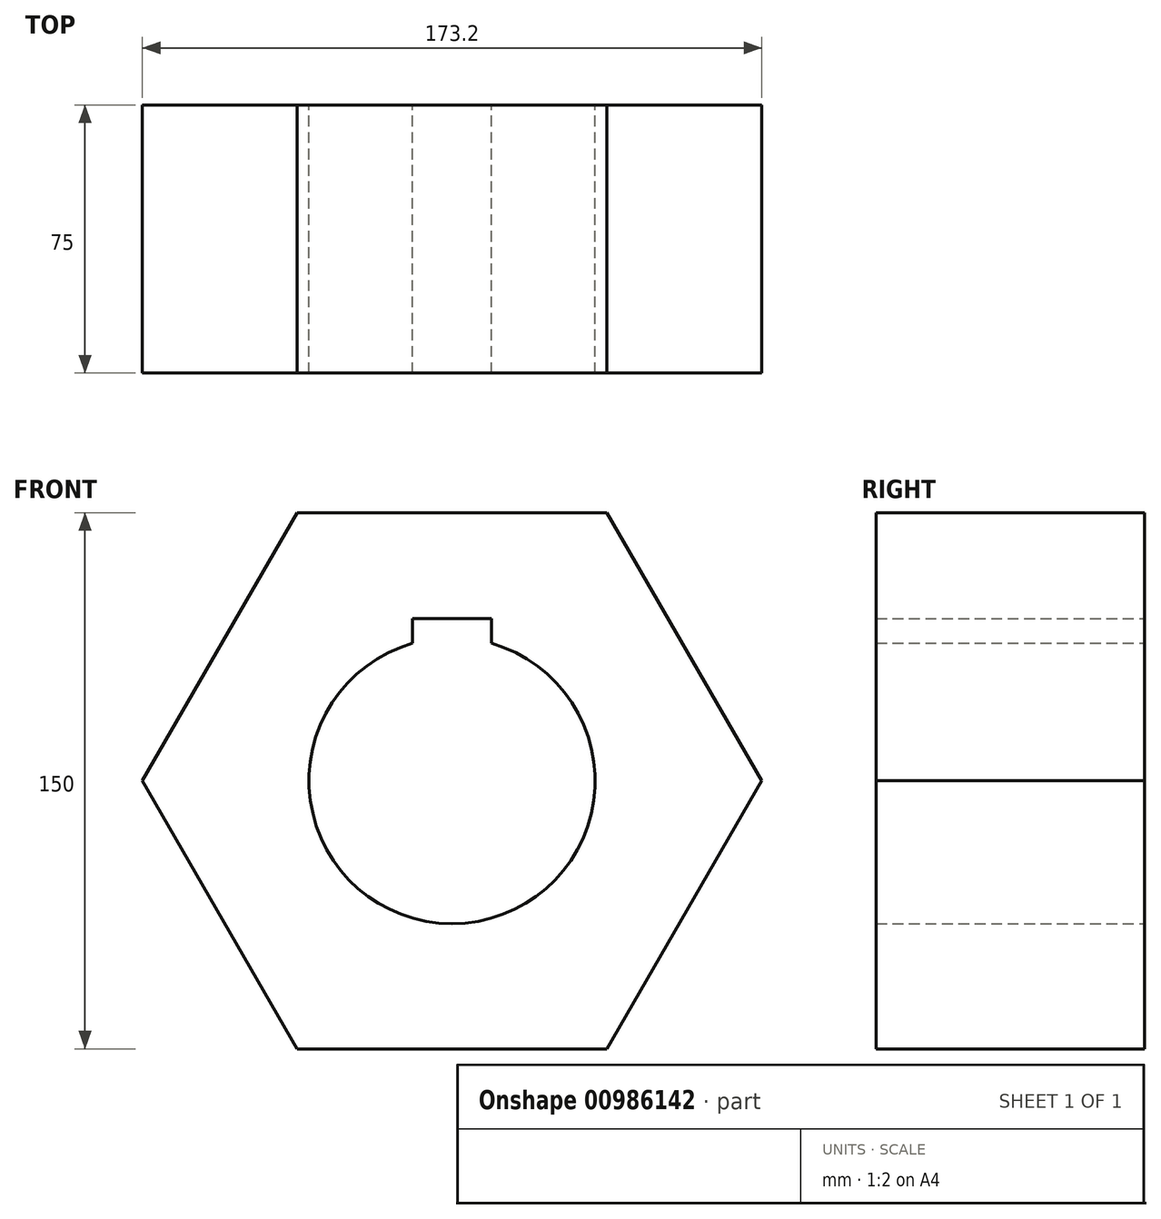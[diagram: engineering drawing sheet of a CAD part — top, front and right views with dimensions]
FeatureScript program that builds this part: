
annotation { "Feature Type Name" : "Feature", "Feature Type Description" : "" }
export const myFeature = defineFeature(function(context is Context, id is Id, definition is map)
    precondition{}
    {
        {
            var Q0;
            Q0=qCreatedBy(makeId("Front.planeOp"),FACE);
            var sketch = newSketch(context, id + "F0", { "sketchPlane" : qUnion([Q0])});
            skCircle(sketch, "E0.cCircle", {"center": v(0, 0) * mm, "radius": 75 * mm, "construction": true});
            skLineSegment(sketch, "E0.0", {"start": v(86.6, 0) * mm, "end": v(43.3, -75) * mm});
            skLineSegment(sketch, "E0.1", {"start": v(43.3, -75) * mm, "end": v(-43.3, -75) * mm});
            skLineSegment(sketch, "E0.2", {"start": v(-43.3, -75) * mm, "end": v(-86.6, 0) * mm});
            skLineSegment(sketch, "E0.3", {"start": v(-86.6, 0) * mm, "end": v(-43.3, 75) * mm});
            skLineSegment(sketch, "E0.4", {"start": v(-43.3, 75) * mm, "end": v(43.3, 75) * mm});
            skLineSegment(sketch, "E0.5", {"start": v(43.3, 75) * mm, "end": v(86.6, 0) * mm});
            skPoint(sketch, "E0.0.midPoint", {"position": v(64.95, -37.5) * mm});
            skArc(sketch, "E1", {"start": v(-11, 38.46) * mm, "mid": v(0, -40) * mm, "end": v(11, 38.46) * mm});
            skLineSegment(sketch, "E2.top", {"start": v(-11, 45.4) * mm, "end": v(11, 45.4) * mm});
            skLineSegment(sketch, "E2.left", {"start": v(-11, 38.46) * mm, "end": v(-11, 45.4) * mm});
            skLineSegment(sketch, "E2.right", {"start": v(11, 38.46) * mm, "end": v(11, 45.4) * mm});
            skPoint(sketch, "E3", {"position": v(0, 45.4) * mm});
            skPoint(sketch, "E4", {"position": v(0, -40) * mm});
            skSolve(sketch);
        }
        {
            var Q0;
            Q0 = qSketchRegion(id + "F0", true);
            extrude(context, id + "F1", {"entities" : qUnion([Q0]), "depth" : 75 * mm, "offsetDistance" : 25 * mm});
        }
    });
